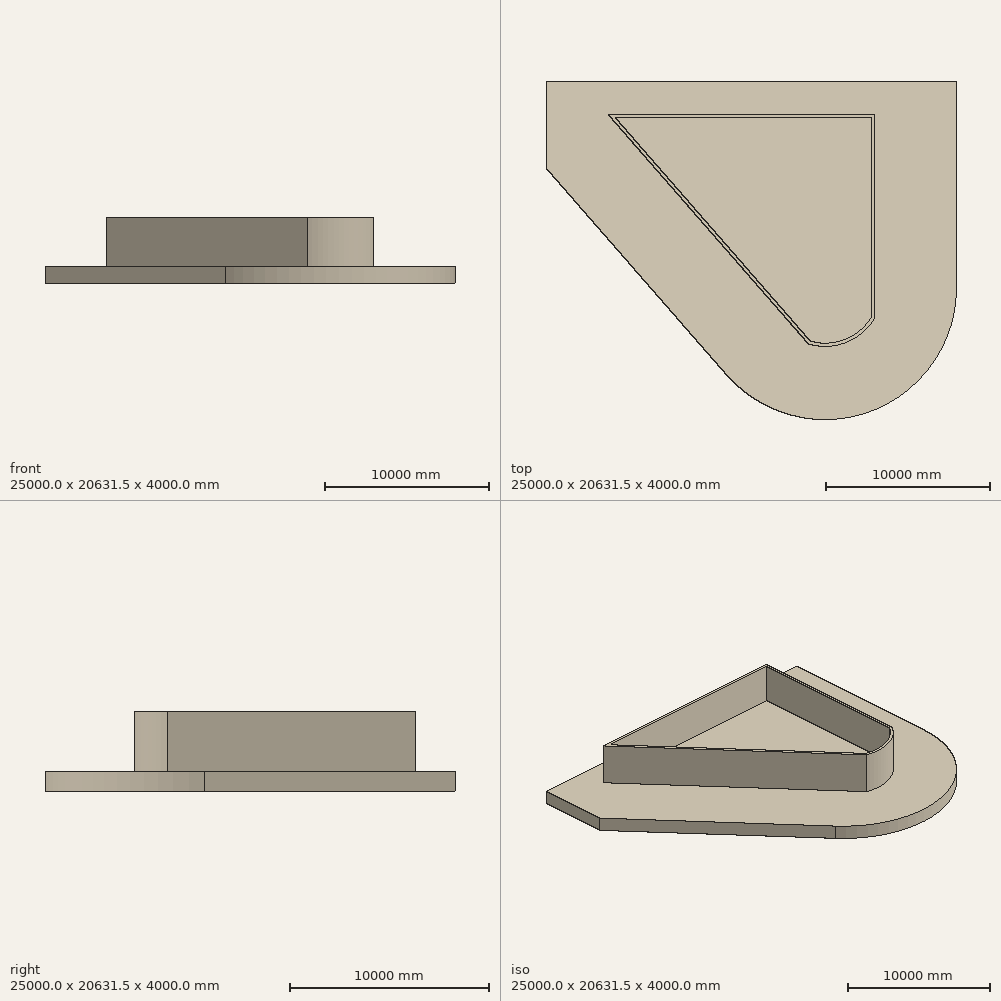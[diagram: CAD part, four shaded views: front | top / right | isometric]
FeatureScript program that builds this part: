
annotation { "Feature Type Name" : "Feature", "Feature Type Description" : "" }
export const myFeature = defineFeature(function(context is Context, id is Id, definition is map)
    precondition{}
    {
        {
            var Q0;
            Q0=qCreatedBy(makeId("Top.planeOp"),FACE);
            var sketch = newSketch(context, id + "F0", { "sketchPlane" : qUnion([Q0])});
            skLineSegment(sketch, "E0", {"start": v(-16974.35, 17893.14) * mm, "end": v(8025.65, 17893.14) * mm});
            skLineSegment(sketch, "E1", {"start": v(8025.65, 17893.14) * mm, "end": v(8025.65, 5263.14) * mm});
            skLineSegment(sketch, "E2", {"start": v(-16974.35, 17893.14) * mm, "end": v(-16974.35, 12573.14) * mm});
            skLineSegment(sketch, "E3", {"start": v(-16974.35, 12573.14) * mm, "end": v(-5998.37, 0) * mm});
            skLineSegment(sketch, "E4", {"start": v(3025.65, 16714.36) * mm, "end": v(3025.65, 9495.35) * mm});
            skLineSegment(sketch, "E5", {"start": v(3025.65, 16714.36) * mm, "end": v(-13212.35, 16714.36) * mm});
            skArc(sketch, "E6", {"start": v(-5998.37, 0) * mm, "mid": v(2837.56, -2228.38) * mm, "end": v(8025.65, 5263.14) * mm});
            skSolve(sketch);
        }
        {
            var Q0;
            Q0=makeQuery(id+"F0.imprint","IMPRINT",FACE,{"disambiguationData":[TD([[makeQuery(id+"F0.imprint","IMPRINT",EDGE,{"derivedFrom":sQuery(id+"F0.wireOp",EDGE,"E0")}),-1.0]])]});
            extrude(context, id + "F1", {"entities" : qUnion([Q0]), "oppositeDirection" : true, "depth" : 1000 * mm, "offsetDistance" : 25 * mm});
        }
        {
            var Q0;
            Q0=makeQuery(id+"F1.opExtrude","CAP_FACE",FACE,{"disambiguationData":[OSD([sQuery(id+"F0.wireOp",EDGE,"E0"),sQuery(id+"F0.wireOp",EDGE,"E1"),sQuery(id+"F0.wireOp",EDGE,"E2"),sQuery(id+"F0.wireOp",EDGE,"E3"),sQuery(id+"F0.wireOp",EDGE,"E6")])],"isStart":true});
            var sketch = newSketch(context, id + "F2", { "sketchPlane" : qUnion([Q0])});
            skLineSegment(sketch, "E7", {"start": v(-13235.45, 15893.14) * mm, "end": v(3025.65, 15893.14) * mm});
            skArc(sketch, "E8", {"start": v(-999.08, 1876.2) * mm, "mid": v(1268.83, 1950.51) * mm, "end": v(3025.65, 3386.67) * mm});
            skLineSegment(sketch, "E9", {"start": v(-13235.45, 15893.14) * mm, "end": v(-999.08, 1876.2) * mm});
            skLineSegment(sketch, "E10", {"start": v(3025.65, 15893.14) * mm, "end": v(3025.65, 3386.67) * mm});
            skSolve(sketch);
        }
        {
            var Q0;
            Q0=makeQuery(id+"F2.imprint","IMPRINT",FACE,{"disambiguationData":[TD([[makeQuery(id+"F2.imprint","IMPRINT",EDGE,{"derivedFrom":sQuery(id+"F2.wireOp",EDGE,"E7")}),-1.0]])]});
            extrude(context, id + "F3", {"entities" : qUnion([Q0]), "depth" : 3000 * mm, "offsetDistance" : 25 * mm});
        }
        {
            var Q0;
            Q0=makeQuery(id+"F3.opExtrude","CAP_FACE",FACE,{"disambiguationData":[OSD([sQuery(id+"F2.wireOp",EDGE,"E7"),sQuery(id+"F2.wireOp",EDGE,"E8"),sQuery(id+"F2.wireOp",EDGE,"E9"),sQuery(id+"F2.wireOp",EDGE,"E10")])],"isStart":false});
            var sketch = newSketch(context, id + "F4", { "sketchPlane" : qUnion([Q0])});
            skSolve(sketch);
        }
        {
            var Q0;
            Q0=makeQuery(id+"F3.opExtrude","CAP_FACE",FACE,{"disambiguationData":[OSD([sQuery(id+"F2.wireOp",EDGE,"E7"),sQuery(id+"F2.wireOp",EDGE,"E8"),sQuery(id+"F2.wireOp",EDGE,"E9"),sQuery(id+"F2.wireOp",EDGE,"E10")])],"isStart":false});
            shell(context, id + "F5", {"entities" : qUnion([Q0]), "thickness" : 200 * mm});
        }
    });
